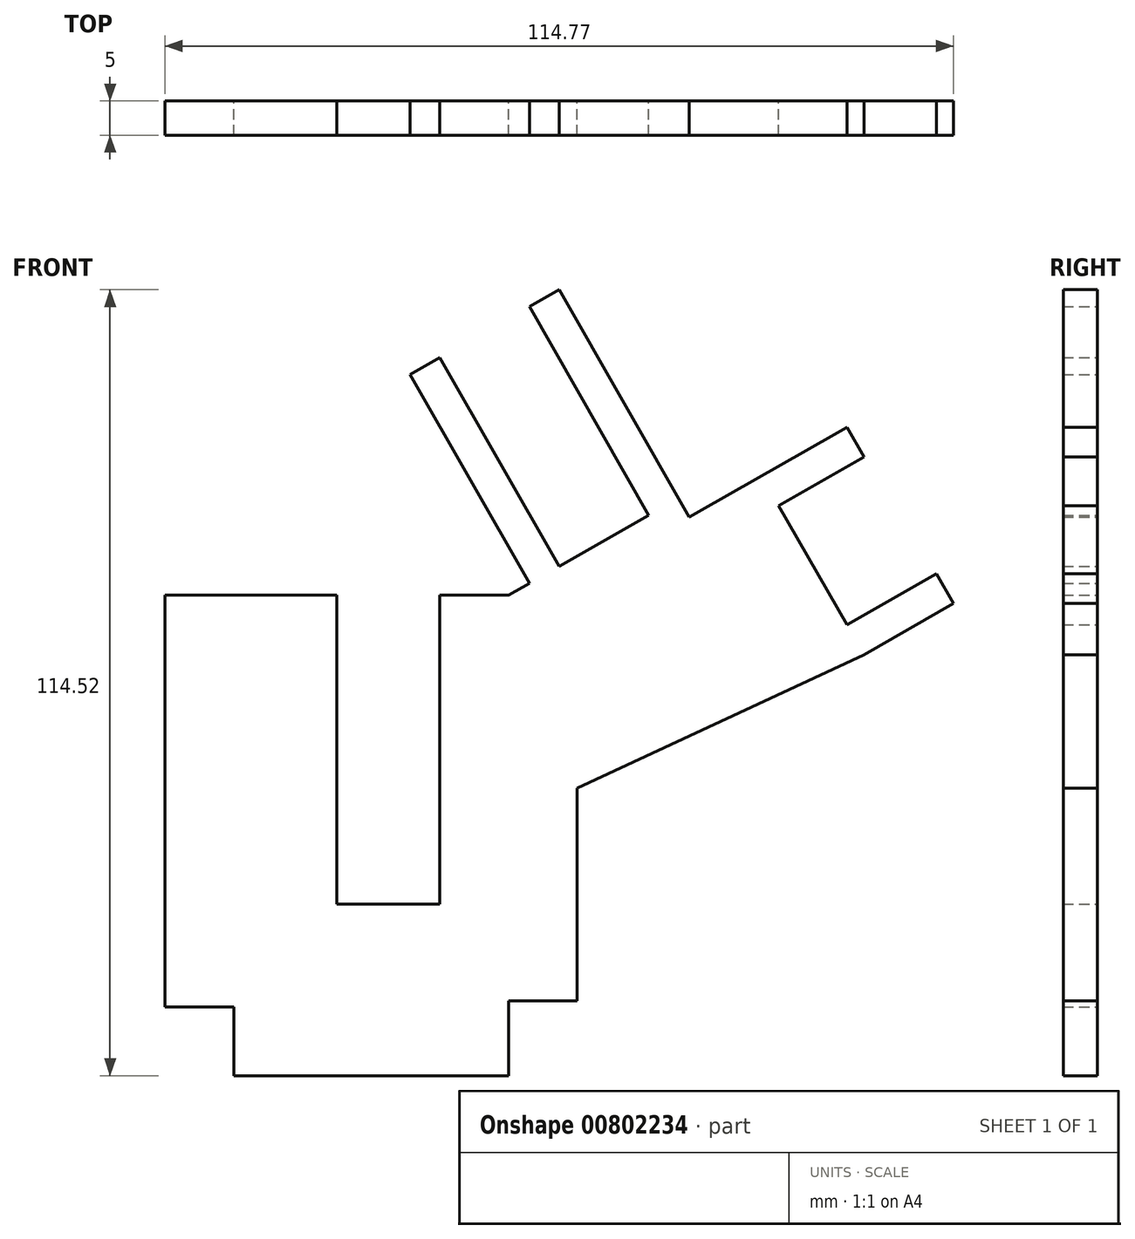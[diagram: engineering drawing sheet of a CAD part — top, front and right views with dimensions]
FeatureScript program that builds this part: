
annotation { "Feature Type Name" : "Feature", "Feature Type Description" : "" }
export const myFeature = defineFeature(function(context is Context, id is Id, definition is map)
    precondition{}
    {
        {
            var Q0;
            Q0=qCreatedBy(makeId("Front.planeOp"),FACE);
            var sketch = newSketch(context, id + "F0", { "sketchPlane" : qUnion([Q0])});
            skLineSegment(sketch, "E0", {"start": v(-19.8, -34.44) * mm, "end": v(20.2, -34.44) * mm});
            skLineSegment(sketch, "E1", {"start": v(20.2, -23.57) * mm, "end": v(20.2, -34.44) * mm});
            skLineSegment(sketch, "E2", {"start": v(-19.8, -34.44) * mm, "end": v(-19.8, -24.44) * mm});
            skLineSegment(sketch, "E3", {"start": v(-19.8, -24.44) * mm, "end": v(-29.8, -24.44) * mm});
            skLineSegment(sketch, "E4", {"start": v(-29.8, -24.44) * mm, "end": v(-29.8, 35.56) * mm});
            skLineSegment(sketch, "E5", {"start": v(-29.8, 35.56) * mm, "end": v(-4.8, 35.56) * mm});
            skLineSegment(sketch, "E6", {"start": v(-4.8, 35.56) * mm, "end": v(-4.8, -9.44) * mm});
            skLineSegment(sketch, "E7", {"start": v(-4.8, -9.44) * mm, "end": v(10.2, -9.44) * mm});
            skLineSegment(sketch, "E8", {"start": v(10.2, -9.44) * mm, "end": v(10.2, 35.56) * mm});
            skLineSegment(sketch, "E9", {"start": v(10.2, 35.56) * mm, "end": v(20.2, 35.56) * mm});
            skLineSegment(sketch, "E10", {"start": v(20.2, 35.56) * mm, "end": v(23.23, 37.29) * mm});
            skLineSegment(sketch, "E11", {"start": v(23.23, 37.29) * mm, "end": v(5.86, 67.68) * mm});
            skLineSegment(sketch, "E12", {"start": v(5.86, 67.68) * mm, "end": v(10.2, 70.16) * mm});
            skLineSegment(sketch, "E13", {"start": v(10.2, 70.16) * mm, "end": v(27.57, 39.77) * mm});
            skLineSegment(sketch, "E14", {"start": v(27.57, 39.77) * mm, "end": v(40.6, 47.2) * mm});
            skLineSegment(sketch, "E15", {"start": v(40.6, 47.2) * mm, "end": v(23.23, 77.6) * mm});
            skLineSegment(sketch, "E16", {"start": v(23.23, 77.6) * mm, "end": v(27.57, 80.08) * mm});
            skLineSegment(sketch, "E17", {"start": v(27.57, 80.08) * mm, "end": v(46.52, 46.91) * mm});
            skLineSegment(sketch, "E18", {"start": v(46.52, 46.91) * mm, "end": v(69.46, 60.02) * mm});
            skLineSegment(sketch, "E19", {"start": v(69.46, 60.02) * mm, "end": v(71.94, 55.68) * mm});
            skLineSegment(sketch, "E20", {"start": v(71.94, 55.68) * mm, "end": v(59.55, 48.6) * mm});
            skLineSegment(sketch, "E21", {"start": v(59.55, 48.6) * mm, "end": v(69.46, 31.24) * mm});
            skLineSegment(sketch, "E22", {"start": v(69.46, 31.24) * mm, "end": v(82.49, 38.69) * mm});
            skLineSegment(sketch, "E23", {"start": v(82.49, 38.69) * mm, "end": v(84.97, 34.34) * mm});
            skLineSegment(sketch, "E24", {"start": v(84.97, 34.34) * mm, "end": v(71.94, 26.9) * mm});
            skLineSegment(sketch, "E25", {"start": v(20.2, -23.57) * mm, "end": v(30.2, -23.57) * mm});
            skLineSegment(sketch, "E26", {"start": v(30.2, -23.57) * mm, "end": v(30.2, 7.44) * mm});
            skLineSegment(sketch, "E27", {"start": v(30.2, 7.44) * mm, "end": v(71.94, 26.9) * mm});
            skSolve(sketch);
        }
        {
            var Q0;
            Q0 = qSketchRegion(id + "F0", true);
            extrude(context, id + "F1", {"entities" : qUnion([Q0]), "depth" : 5 * mm, "offsetDistance" : 25 * mm});
        }
    });
